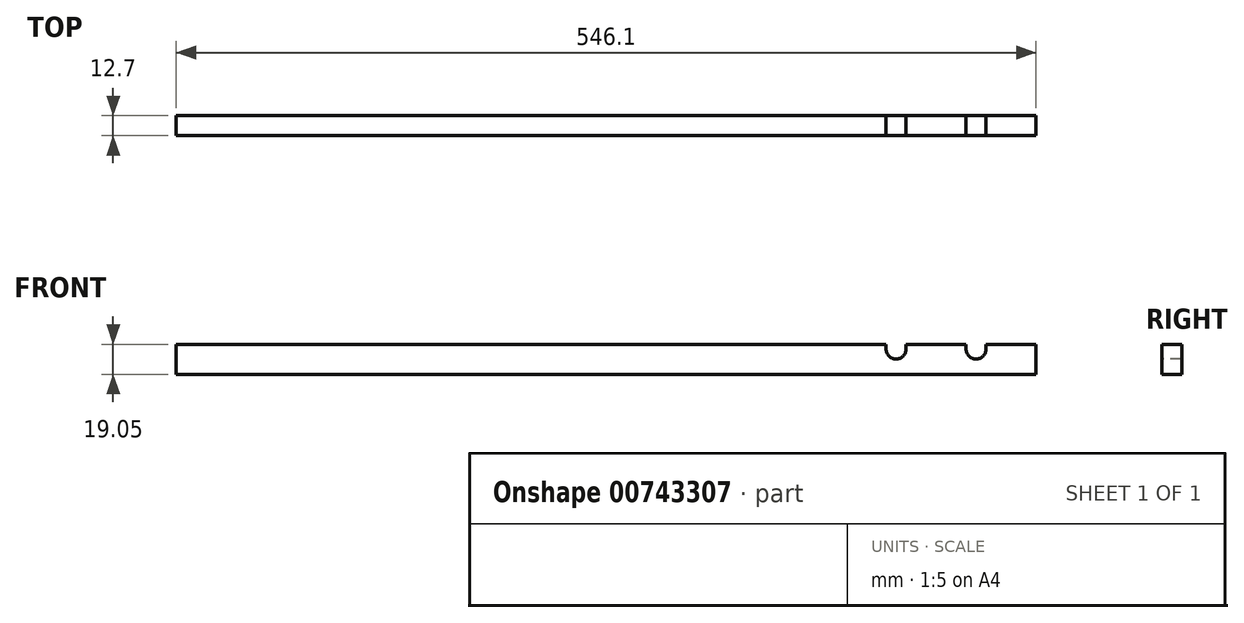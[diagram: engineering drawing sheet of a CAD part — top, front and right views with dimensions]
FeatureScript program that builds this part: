
annotation { "Feature Type Name" : "Feature", "Feature Type Description" : "" }
export const myFeature = defineFeature(function(context is Context, id is Id, definition is map)
    precondition{}
    {
        {
            var Q0;
            Q0=qCreatedBy(makeId("Front.planeOp"),FACE);
            var sketch = newSketch(context, id + "F0", { "sketchPlane" : qUnion([Q0])});
            skLineSegment(sketch, "E0.bottom", {"start": v(-76.14, 12.05) * mm, "end": v(469.96, 12.05) * mm});
            skLineSegment(sketch, "E0.top", {"start": v(-76.14, -7) * mm, "end": v(469.96, -7) * mm});
            skLineSegment(sketch, "E0.left", {"start": v(-76.14, 12.05) * mm, "end": v(-76.14, -7) * mm});
            skLineSegment(sketch, "E0.right", {"start": v(469.96, 12.05) * mm, "end": v(469.96, -7) * mm});
            skSolve(sketch);
        }
        {
            var Q0;
            Q0=makeQuery(id+"F0.imprint","IMPRINT",FACE,{"disambiguationData":[TD([[makeQuery(id+"F0.imprint","IMPRINT",EDGE,{"derivedFrom":sQuery(id+"F0.wireOp",EDGE,"E0.bottom")}),-1.0]])]});
            extrude(context, id + "F1", {"entities" : qUnion([Q0]), "depth" : 12.7 * mm, "offsetDistance" : 25.4 * mm});
        }
        {
            var Q0;
            Q0=makeQuery(id+"F1.opExtrude","CAP_FACE",FACE,{"disambiguationData":[OSD([sQuery(id+"F0.wireOp",EDGE,"E0.bottom"),sQuery(id+"F0.wireOp",EDGE,"E0.top"),sQuery(id+"F0.wireOp",EDGE,"E0.left"),sQuery(id+"F0.wireOp",EDGE,"E0.right")])],"isStart":false});
            var sketch = newSketch(context, id + "F2", { "sketchPlane" : qUnion([Q0])});
            skPoint(sketch, "E1", {"position": v(431.86, 9) * mm});
            skPoint(sketch, "E2", {"position": v(381.06, 9) * mm});
            skPoint(sketch, "E3", {"position": v(469.96, 9) * mm});
            skCircle(sketch, "E4", {"center": v(381.06, 9) * mm, "radius": 6.35 * mm});
            skPoint(sketch, "E5", {"position": v(469.96, 12.05) * mm});
            skLineSegment(sketch, "E6", {"start": v(374.71, 9) * mm, "end": v(374.71, 12.05) * mm});
            skLineSegment(sketch, "E7", {"start": v(374.71, 12.05) * mm, "end": v(387.41, 12.05) * mm});
            skLineSegment(sketch, "E8", {"start": v(387.41, 12.05) * mm, "end": v(387.41, 9) * mm});
            skCircle(sketch, "E9", {"center": v(431.86, 9) * mm, "radius": 6.35 * mm});
            skPoint(sketch, "E10", {"position": v(425.51, 12.05) * mm});
            skPoint(sketch, "E11", {"position": v(438.21, 12.05) * mm});
            skPoint(sketch, "E12", {"position": v(438.21, 9) * mm});
            skPoint(sketch, "E13", {"position": v(425.51, 9) * mm});
            skLineSegment(sketch, "E14", {"start": v(425.51, 12.05) * mm, "end": v(425.51, 9) * mm});
            skLineSegment(sketch, "E15", {"start": v(438.21, 12.05) * mm, "end": v(438.21, 9) * mm});
            skSolve(sketch);
        }
        {
            var Q0;
            {var subQ0=sQuery(id+"F2.wireOp",EDGE,"E6");Q0=makeQuery(id+"F2.imprint","IMPRINT",FACE,{"disambiguationData":[TD([[makeQuery(id+"F2.imprint","IMPRINT",EDGE,{"derivedFrom":subQ0}),-1.0]])]});}
            var Q1;
            {var subQ0=sQuery(id+"F2.wireOp",EDGE,"E4");var subQ1=makeQuery(id+"F2.imprint","INTERSECT",VERTEX,{"derivedFrom":[subQ0,sQuery(id+"F2.wireOp",EDGE,"E6")]});Q1=makeQuery(id+"F2.imprint","IMPRINT",FACE,{"disambiguationData":[TD([[makeQuery(id+"F2.imprint","IMPRINT",EDGE,{"disambiguationData":[TD([[subQ1,1.0]])],"derivedFrom":subQ0}),1.0]])]});}
            var Q2;
            {var subQ0=sQuery(id+"F2.wireOp",EDGE,"E14");Q2=makeQuery(id+"F2.imprint","IMPRINT",FACE,{"disambiguationData":[TD([[makeQuery(id+"F2.imprint","IMPRINT",EDGE,{"derivedFrom":subQ0}),1.0]])]});}
            var Q3;
            {var subQ0=sQuery(id+"F2.wireOp",EDGE,"E9");var subQ1=makeQuery(id+"F2.imprint","INTERSECT",VERTEX,{"derivedFrom":[subQ0,sQuery(id+"F2.wireOp",EDGE,"E15")]});Q3=makeQuery(id+"F2.imprint","IMPRINT",FACE,{"disambiguationData":[TD([[makeQuery(id+"F2.imprint","IMPRINT",EDGE,{"disambiguationData":[TD([[subQ1,-1.0]])],"derivedFrom":subQ0}),1.0]])]});}
            var Q4;
            {var subQ0=sQuery(id+"F2.wireOp",EDGE,"E15");Q4=makeQuery(id+"F2.imprint","IMPRINT",FACE,{"disambiguationData":[TD([[makeQuery(id+"F2.imprint","IMPRINT",EDGE,{"derivedFrom":subQ0}),-1.0]])]});}
            var Q5;
            {var subQ0=sQuery(id+"F2.wireOp",EDGE,"E8");Q5=makeQuery(id+"F2.imprint","IMPRINT",FACE,{"disambiguationData":[TD([[makeQuery(id+"F2.imprint","IMPRINT",EDGE,{"derivedFrom":subQ0}),-1.0]])]});}
            extrude(context, id + "F3", {"entities" : qUnion([Q0, Q1, Q2, Q3, Q4, Q5]), "operationType" : NewBodyOperationType.REMOVE, "oppositeDirection" : true, "depth" : 25.4 * mm, "offsetDistance" : 25.4 * mm});
        }
    });
